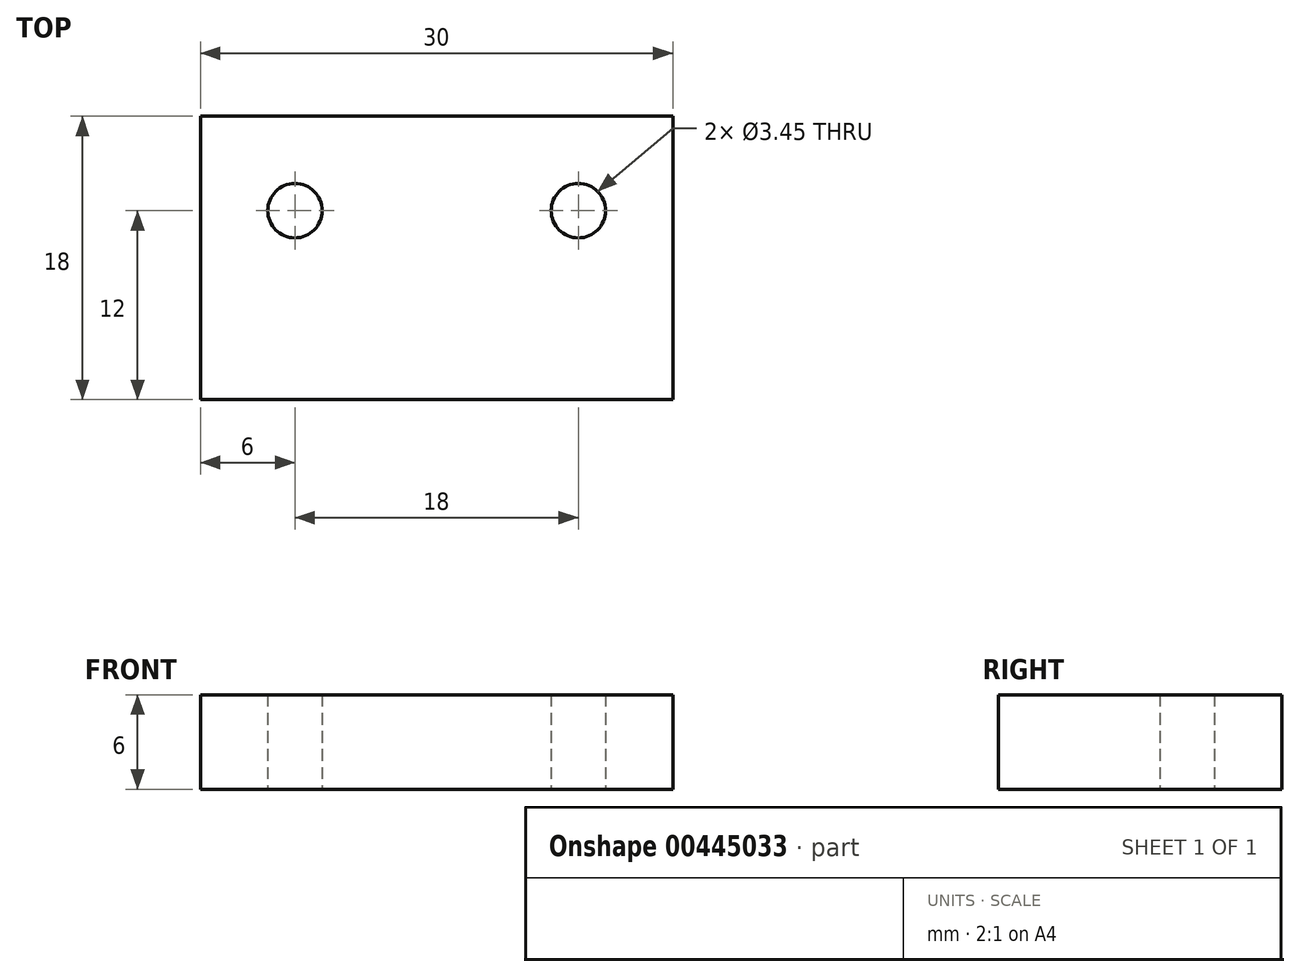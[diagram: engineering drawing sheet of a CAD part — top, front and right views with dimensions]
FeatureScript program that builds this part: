
annotation { "Feature Type Name" : "Feature", "Feature Type Description" : "" }
export const myFeature = defineFeature(function(context is Context, id is Id, definition is map)
    precondition{}
    {
        {
            var Q0;
            Q0=qCreatedBy(makeId("Top.planeOp"),FACE);
            var sketch = newSketch(context, id + "F0", { "sketchPlane" : qUnion([Q0])});
            skLineSegment(sketch, "E0.bottom", {"start": v(-15, 9) * mm, "end": v(15, 9) * mm});
            skLineSegment(sketch, "E0.top", {"start": v(-15, -9) * mm, "end": v(15, -9) * mm});
            skLineSegment(sketch, "E0.left", {"start": v(-15, 9) * mm, "end": v(-15, -9) * mm});
            skLineSegment(sketch, "E0.right", {"start": v(15, 9) * mm, "end": v(15, -9) * mm});
            skPoint(sketch, "E1", {"position": v(-15, 0) * mm});
            skPoint(sketch, "E2", {"position": v(0, 9) * mm});
            skCircle(sketch, "E3", {"center": v(-9, 3) * mm, "radius": 1.73 * mm});
            skCircle(sketch, "E4", {"center": v(9, 3) * mm, "radius": 1.73 * mm});
            skSolve(sketch);
        }
        {
            var Q0;
            Q0 = qSketchRegion(id + "F0", true);
            extrude(context, id + "F1", {"entities" : qUnion([Q0]), "depth" : 6 * mm});
        }
    });
